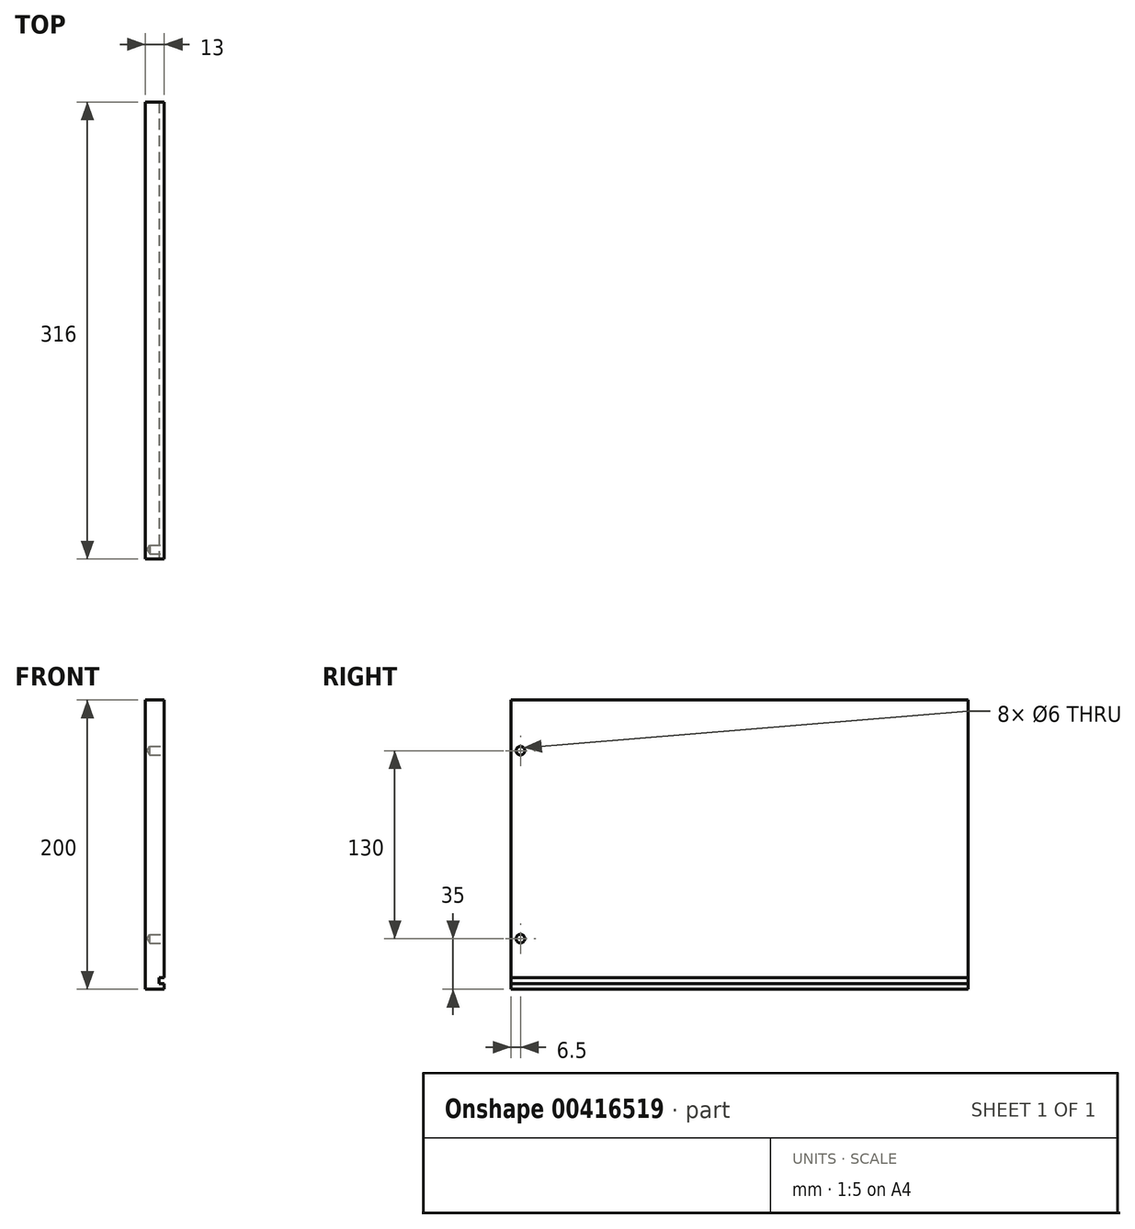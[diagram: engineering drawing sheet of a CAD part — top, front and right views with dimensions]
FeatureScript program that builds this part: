
annotation { "Feature Type Name" : "Feature", "Feature Type Description" : "" }
export const myFeature = defineFeature(function(context is Context, id is Id, definition is map)
    precondition{}
    {
        {
            var Q0;
            Q0=qCreatedBy(makeId("Front.planeOp"),FACE);
            var sketch = newSketch(context, id + "F0", { "sketchPlane" : qUnion([Q0])});
            skLineSegment(sketch, "E0.bottom", {"start": v(-6.5, 100) * mm, "end": v(6.5, 100) * mm});
            skLineSegment(sketch, "E0.top", {"start": v(-6.5, -100) * mm, "end": v(6.5, -100) * mm});
            skLineSegment(sketch, "E0.right", {"start": v(6.5, 100) * mm, "end": v(6.5, -92) * mm});
            skPoint(sketch, "E0.middle", {"position": v(0, 0) * mm});
            skLineSegment(sketch, "E1", {"start": v(-6.5, 100) * mm, "end": v(-6.5, -100) * mm});
            skLineSegment(sketch, "E2", {"start": v(6.5, -96) * mm, "end": v(2.88, -96) * mm});
            skLineSegment(sketch, "E3", {"start": v(2.88, -96) * mm, "end": v(2.88, -92) * mm});
            skLineSegment(sketch, "E4", {"start": v(2.88, -92) * mm, "end": v(6.5, -92) * mm});
            skLineSegment(sketch, "E5", {"start": v(6.5, -96) * mm, "end": v(6.5, -100) * mm});
            skSolve(sketch);
        }
        {
            var Q0;
            Q0=qSketchRegion(id+"F0",true);
            extrude(context, id + "F1", {"entities" : qUnion([Q0]), "endBound" : BoundingType.SYMMETRIC, "oppositeDirection" : true, "depth" : 316 * mm});
        }
        {
            var Q0;
            Q0=makeQuery(id+"F1.opExtrude","SWEPT_FACE",FACE,{"disambiguationData":[OSD([sQuery(id+"F0.wireOp",EDGE,"E0.right")])]});
            var sketch = newSketch(context, id + "F2", { "sketchPlane" : qUnion([Q0])});
            skPoint(sketch, "E6", {"position": v(-151.5, 65) * mm});
            skPoint(sketch, "E7", {"position": v(-151.5, -65) * mm});
            skLineSegment(sketch, "E8", {"start": v(-151.5, 72.2) * mm, "end": v(-151.5, -82.92) * mm, "construction": true});
            skSolve(sketch);
        }
        {
            var Q0;
            Q0=sQuery(id+"F2.wireOp",VERTEX,"E6");
            var Q1;
            Q1=sQuery(id+"F2.wireOp",VERTEX,"E7");
            var Q2;
            Q2=makeQuery(id+"F1.opExtrude","SWEPT_BODY",BODY,{"disambiguationData":[OSD([sQuery(id+"F0.wireOp",EDGE,"E0.bottom"),sQuery(id+"F0.wireOp",EDGE,"E0.top"),sQuery(id+"F0.wireOp",EDGE,"E0.right"),sQuery(id+"F0.wireOp",EDGE,"E1"),sQuery(id+"F0.wireOp",EDGE,"E2"),sQuery(id+"F0.wireOp",EDGE,"E3"),sQuery(id+"F0.wireOp",EDGE,"E4"),sQuery(id+"F0.wireOp",EDGE,"E5")])]});
            hole(context, id + "F3", {"style" : HoleStyle.SIMPLE, "endStyle" : HoleEndStyle.BLIND, "holeDiameter" : 6 * mm, "holeDepth" : 10 * mm, "isTappedThrough" : true, "tappedDepth" : 12 * mm, "tapClearance" : 3, "startFromSketch" : true, "locations" : qUnion([Q0, Q1]), "scope" : qUnion([Q2])});
        }
    });
